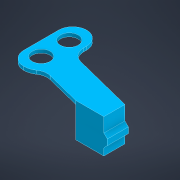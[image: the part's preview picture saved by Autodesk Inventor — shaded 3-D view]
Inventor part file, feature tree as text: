
AUTODESK INVENTOR PART (.ipt)
format: ipt  version: 2022 (Build 260153000, 153)  size: 429,056 bytes
history: native  units: in
note: dims shown in document units (in); Inventor stores cm internally (conversion verified against a paired STEP export)
features: extrude x7, sketch x7, projected_geometry x4, chamfer x2, fillet x1
ambient origin geometry x8: Origin, YZ Plane, XZ Plane, XY Plane, X Axis, Y Axis, Z Axis, Center Point
bodies: Solid1 (feature_tree)
feature tree (21):
  extrude  "Extrusion1"  Depth=0.722in
  extrude  "Extrusion2"  Depth=1.0in
  extrude  "Extrusion3"  Depth=0.375in TaperAngle=0.0deg
  extrude  "Extrusion4"  Depth=3.0in
  fillet  "Fillet1"  Radius=1.75in
  extrude  "Extrusion5"  Depth=0.64in
  chamfer  "Chamfer1"  Distance=0.125in
  extrude  "Extrusion6"  Depth=0.125in TaperAngle=0.0deg
  extrude  "Extrusion7"  Depth=0.125in TaperAngle=45.0deg
  chamfer  "Chamfer2"  Distance=0.156in
  sketch  "Sketch1"  dims[d0=0.125in d1=0.722in]
  sketch  "Sketch2"  dims[d2=0.63in d3=0.0in d4=1.0in]
  projected_geometry  "Projected Loop1"
  sketch  "Sketch3"  dims[d5=0.125in d6=0.0in d7=0.375in d8=0.0in]
  sketch  "Sketch4"  dims[d9=0.5in d10=3.0in d11=1.75in]
  sketch  "Sketch5"  dims[d12=1.0in d13=0.64in]
  sketch  "Sketch6"  dims[d14=0.504in d15=0.125in d16=0.0in]
  projected_geometry  "Projected Loop2"
  projected_geometry  "Projected Loop3"
  sketch  "Sketch7"  dims[d17=0.5in d18=0.125in d19=0.0in d20=0.125in d21=0.125in d22=45.0deg d23=0.156in d24=0.08in d25=0.0in d26=0.5in d27=0.0in d28=0.125in d29=0.0in d30=0.125in d31=0.125in d32=45.0deg]
  projected_geometry  "Projected Loop4"
